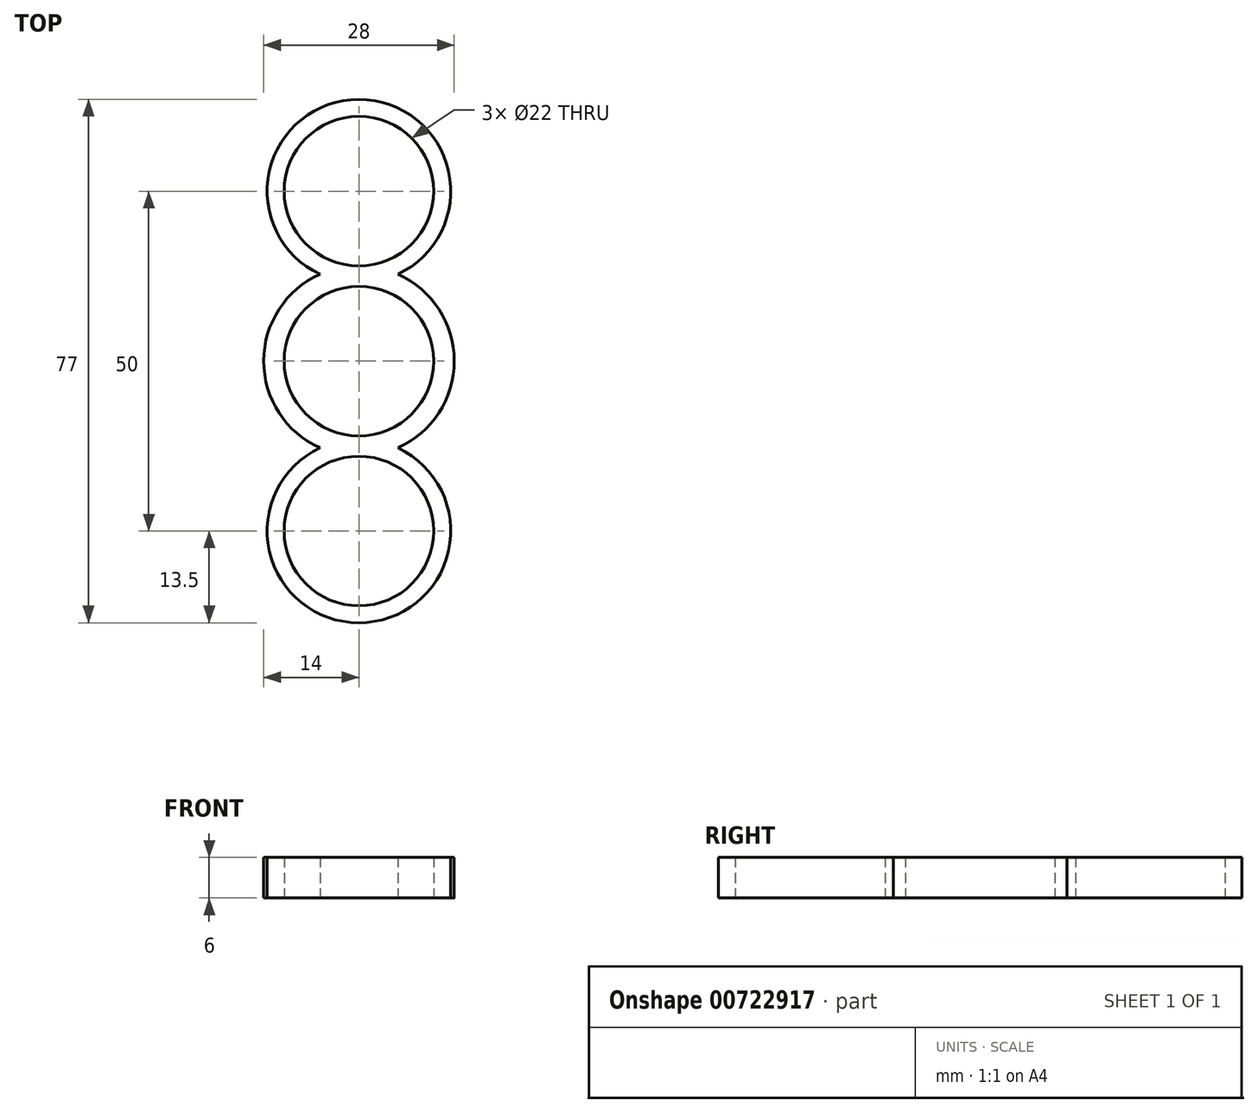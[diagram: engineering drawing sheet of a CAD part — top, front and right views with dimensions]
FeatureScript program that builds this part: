
annotation { "Feature Type Name" : "Feature", "Feature Type Description" : "" }
export const myFeature = defineFeature(function(context is Context, id is Id, definition is map)
    precondition{}
    {
        {
            var Q0;
            Q0=qCreatedBy(makeId("Top.planeOp"),FACE);
            var sketch = newSketch(context, id + "F0", { "sketchPlane" : qUnion([Q0])});
            skCircle(sketch, "E0", {"center": v(0, 0) * mm, "radius": 11 * mm});
            skLineSegment(sketch, "E1", {"start": v(0, 0) * mm, "end": v(0, 25) * mm});
            skCircle(sketch, "E2", {"center": v(0, 25) * mm, "radius": 11 * mm});
            skLineSegment(sketch, "E3", {"start": v(0, 0) * mm, "end": v(0, -25) * mm});
            skCircle(sketch, "E4", {"center": v(0, -25) * mm, "radius": 11 * mm});
            skArc(sketch, "E5", {"start": v(5.73, 12.78) * mm, "mid": v(0, 38.5) * mm, "end": v(-5.73, 12.78) * mm});
            skArc(sketch, "E6", {"start": v(-5.73, 12.78) * mm, "mid": v(-14, 0) * mm, "end": v(-5.73, -12.78) * mm});
            skArc(sketch, "E7", {"start": v(-5.73, -12.78) * mm, "mid": v(0, -38.5) * mm, "end": v(5.73, -12.78) * mm});
            skArc(sketch, "E8.trimOffspring", {"start": v(5.73, -12.78) * mm, "mid": v(14, 0) * mm, "end": v(5.73, 12.78) * mm});
            skSolve(sketch);
        }
        {
            var Q0;
            Q0 = qSketchRegion(id + "F0", true);
            extrude(context, id + "F1", {"entities" : qUnion([Q0]), "depth" : 6 * mm, "offsetDistance" : 25 * mm});
        }
    });
